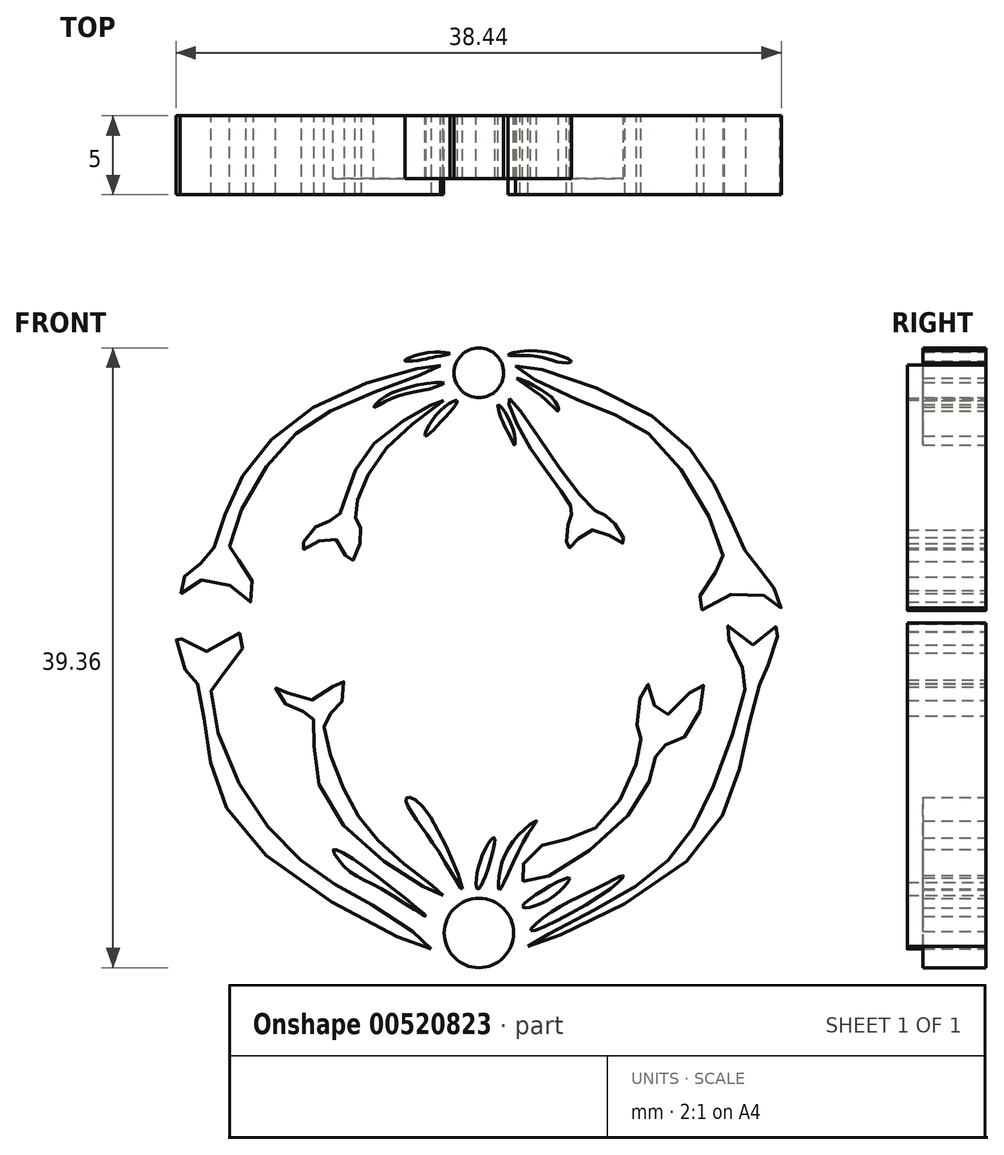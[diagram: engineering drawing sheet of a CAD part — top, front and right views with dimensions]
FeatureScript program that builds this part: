
annotation { "Feature Type Name" : "Feature", "Feature Type Description" : "" }
export const myFeature = defineFeature(function(context is Context, id is Id, definition is map)
    precondition{}
    {
        {
            var Q0;
            Q0=qCreatedBy(makeId("Front.planeOp"),FACE);
            var sketch = newSketch(context, id + "F0", { "sketchPlane" : qUnion([Q0])});
            skLineSegment(sketch, "E0", {"start": v(0, 0) * mm, "end": v(0, 40) * mm});
            skSolve(sketch);
        }
        {
            var Q0;
            Q0=qCreatedBy(makeId("Front.planeOp"),FACE);
            var sketch = newSketch(context, id + "F1", { "sketchPlane" : qUnion([Q0])});
            skArc(sketch, "E1", {"start": v(0, 0) * mm, "mid": v(19.9, 19.93) * mm, "end": v(0, 39.86) * mm});
            skSolve(sketch);
        }
        {
            var Q0;
            Q0=sQuery(id+"F1.wireOp",EDGE,"E1");
            var Q1;
            Q1=sQuery(id+"F0.wireOp",EDGE,"E0");
            revolve(context, id + "F2", {"bodyType" : ToolBodyType.SURFACE, "surfaceEntities" : qUnion([Q0]), "axis" : qUnion([Q1]), "revolveType" : RevolveType.TWO_DIRECTIONS, "angle" : 179.35 * degree, "angleBack" : 1.4 * degree});
        }
        {
            var Q0;
            Q0=qCreatedBy(makeId("Front.planeOp"),FACE);
            var sketch = newSketch(context, id + "F3", { "sketchPlane" : qUnion([Q0])});
            skCircle(sketch, "E2", {"center": v(0, 2.34) * mm, "radius": 2.2 * mm});
            skSolve(sketch);
        }
        {
            var Q0;
            Q0=makeQuery(id+"F3.imprint","IMPRINT",FACE,{"disambiguationData":[TD([[makeQuery(id+"F3.imprint","IMPRINT",EDGE,{"derivedFrom":sQuery(id+"F3.wireOp",EDGE,"E2")}),1.0]])]});
            extrude(context, id + "F4", {"entities" : qUnion([Q0]), "depth" : 4 * mm, "offsetDistance" : 25 * mm});
        }
        {
            var Q0;
            Q0=qCreatedBy(makeId("Front.planeOp"),FACE);
            var sketch = newSketch(context, id + "F5", { "sketchPlane" : qUnion([Q0])});
            skCircle(sketch, "E3", {"center": v(0, 37.92) * mm, "radius": 1.58 * mm});
            skSolve(sketch);
        }
        {
            var Q0;
            Q0=makeQuery(id+"F5.imprint","IMPRINT",FACE,{"disambiguationData":[TD([[makeQuery(id+"F5.imprint","IMPRINT",EDGE,{"derivedFrom":sQuery(id+"F5.wireOp",EDGE,"E3")}),1.0]])]});
            extrude(context, id + "F6", {"entities" : qUnion([Q0]), "depth" : 4 * mm, "offsetDistance" : 25 * mm});
        }
        {
            var Q0;
            Q0=qCreatedBy(makeId("Front.planeOp"),FACE);
            var sketch = newSketch(context, id + "F7", { "sketchPlane" : qUnion([Q0])});
            skFitSpline(sketch, "E4", {"points": [v(2.8, 5.61) * mm, v(10.25, 10.8) * mm, v(11.49, 14.06) * mm, v(13.34, 15.07) * mm, v(14.11, 18.2) * mm, v(11.61, 16.13) * mm, v(10.72, 18.16) * mm, v(10.01, 15.74) * mm, v(10.3, 14.49) * mm, v(7.37, 8.98) * mm, v(3.55, 7.63) * mm, v(2.8, 5.61) * mm]});
            skSolve(sketch);
        }
        {
            var Q0;
            Q0=makeQuery(id+"F7.imprint","IMPRINT",FACE,{"disambiguationData":[TD([[makeQuery(id+"F7.imprint","IMPRINT",EDGE,{"derivedFrom":sQuery(id+"F7.wireOp",EDGE,"E4")}),1.0]])]});
            extrude(context, id + "F8", {"entities" : qUnion([Q0]), "depth" : 5 * mm, "offsetDistance" : 25 * mm});
        }
        {
            var Q0;
            Q0=qCreatedBy(makeId("Front.planeOp"),FACE);
            var sketch = newSketch(context, id + "F9", { "sketchPlane" : qUnion([Q0])});
            skFitSpline(sketch, "E5", {"points": [v(-2.25, 36.18) * mm, v(-7.2, 32.8) * mm, v(-8.95, 28.8) * mm, v(-10.37, 28.13) * mm, v(-11.23, 26.7) * mm, v(-9.3, 27.44) * mm, v(-8.17, 25.93) * mm, v(-7.46, 27.8) * mm, v(-7.83, 28.66) * mm, v(-5.82, 33.2) * mm, v(-2.25, 36.18) * mm]});
            skSolve(sketch);
        }
        {
            var Q0;
            Q0=qCreatedBy(makeId("Front.planeOp"),FACE);
            var sketch = newSketch(context, id + "F10", { "sketchPlane" : qUnion([Q0])});
            skFitSpline(sketch, "E6", {"points": [v(-3.05, 1.35) * mm, v(-13.8, 7.53) * mm, v(-17.31, 14.74) * mm, v(-18.05, 18.51) * mm, v(-18.8, 19.3) * mm, v(-19.2, 21.5) * mm, v(-17.99, 20.17) * mm, v(-14.91, 21.45) * mm, v(-15.64, 19.34) * mm, v(-16.89, 18.24) * mm, v(-15.48, 12.3) * mm, v(-10.79, 6.54) * mm, v(-6.03, 3.66) * mm, v(-3.05, 1.35) * mm]});
            skSolve(sketch);
        }
        {
            var Q0;
            Q0=qCreatedBy(makeId("Front.planeOp"),FACE);
            var sketch = newSketch(context, id + "F11", { "sketchPlane" : qUnion([Q0])});
            skFitSpline(sketch, "E7", {"points": [v(-2.29, 4.72) * mm, v(-9.68, 10.66) * mm, v(-10.63, 16.2) * mm, v(-11.97, 16.64) * mm, v(-12.88, 17.97) * mm, v(-10.66, 17.13) * mm, v(-8.69, 18.42) * mm, v(-8.84, 16.76) * mm, v(-9.74, 16) * mm, v(-8.6, 11.55) * mm, v(-5.28, 7.16) * mm, v(-2.29, 4.72) * mm]});
            skSolve(sketch);
        }
        {
            var Q0;
            Q0=qCreatedBy(makeId("Front.planeOp"),FACE);
            var sketch = newSketch(context, id + "F12", { "sketchPlane" : qUnion([Q0])});
            skFitSpline(sketch, "E8", {"points": [v(3.12, 1.48) * mm, v(12.95, 6.68) * mm, v(16.85, 14.18) * mm, v(18.02, 18.66) * mm, v(18.55, 19.78) * mm, v(19.07, 22.03) * mm, v(17.52, 20.65) * mm, v(15.64, 21.98) * mm, v(16.5, 19.58) * mm, v(16.96, 18.56) * mm, v(15.06, 12.06) * mm, v(11.96, 6.9) * mm, v(6.67, 3.46) * mm, v(3.12, 1.48) * mm]});
            skSolve(sketch);
        }
        {
            var Q0;
            Q0=makeQuery(id+"F10.imprint","IMPRINT",FACE,{"disambiguationData":[TD([[makeQuery(id+"F10.imprint","IMPRINT",EDGE,{"derivedFrom":sQuery(id+"F10.wireOp",EDGE,"E6")}),-1.0]])]});
            extrude(context, id + "F13", {"entities" : qUnion([Q0]), "depth" : 5 * mm, "offsetDistance" : 25 * mm});
        }
        {
            var Q0;
            Q0=makeQuery(id+"F11.imprint","IMPRINT",FACE,{"disambiguationData":[TD([[makeQuery(id+"F11.imprint","IMPRINT",EDGE,{"derivedFrom":sQuery(id+"F11.wireOp",EDGE,"E7")}),-1.0]])]});
            extrude(context, id + "F14", {"entities" : qUnion([Q0]), "depth" : 5 * mm, "offsetDistance" : 25 * mm});
        }
        {
            var Q0;
            Q0=makeQuery(id+"F12.imprint","IMPRINT",FACE,{"disambiguationData":[TD([[makeQuery(id+"F12.imprint","IMPRINT",EDGE,{"derivedFrom":sQuery(id+"F12.wireOp",EDGE,"E8")}),1.0]])]});
            extrude(context, id + "F15", {"entities" : qUnion([Q0]), "depth" : 5 * mm, "offsetDistance" : 25 * mm});
        }
        {
            var Q0;
            Q0=qCreatedBy(makeId("Front.planeOp"),FACE);
            var sketch = newSketch(context, id + "F16", { "sketchPlane" : qUnion([Q0])});
            skFitSpline(sketch, "E9", {"points": [v(-2.43, 38.38) * mm, v(-9.35, 36.35) * mm, v(-15.72, 29.99) * mm, v(-17.26, 26.1) * mm, v(-18.44, 25.37) * mm, v(-18.94, 23.93) * mm, v(-16.87, 24.94) * mm, v(-14.47, 23.38) * mm, v(-14.8, 25.68) * mm, v(-15.78, 26.43) * mm, v(-13.3, 32.25) * mm, v(-7.5, 36.36) * mm, v(-2.43, 38.38) * mm]});
            skSolve(sketch);
        }
        {
            var Q0;
            Q0=qCreatedBy(makeId("Front.planeOp"),FACE);
            var sketch = newSketch(context, id + "F17", { "sketchPlane" : qUnion([Q0])});
            skFitSpline(sketch, "E10", {"points": [v(1.95, 36.3) * mm, v(7.08, 29.43) * mm, v(8.37, 28.63) * mm, v(9.24, 27.1) * mm, v(7.16, 27.94) * mm, v(5.7, 26.8) * mm, v(5.7, 28.47) * mm, v(5.88, 29.31) * mm, v(2.98, 33.63) * mm, v(1.95, 36.3) * mm]});
            skSolve(sketch);
        }
        {
            var Q0;
            Q0=qCreatedBy(makeId("Front.planeOp"),FACE);
            var sketch = newSketch(context, id + "F18", { "sketchPlane" : qUnion([Q0])});
            skFitSpline(sketch, "E11", {"points": [v(2.32, 38.37) * mm, v(10.39, 35.55) * mm, v(15.47, 29.79) * mm, v(17.3, 26.03) * mm, v(18.48, 24.67) * mm, v(19.19, 23) * mm, v(17.16, 24.1) * mm, v(13.93, 22.85) * mm, v(14.7, 24.9) * mm, v(15.52, 26.04) * mm, v(11.61, 33.29) * mm, v(6.44, 36.13) * mm, v(2.32, 38.37) * mm]});
            skSolve(sketch);
        }
        {
            var Q0;
            Q0=makeQuery(id+"F18.imprint","IMPRINT",FACE,{"disambiguationData":[TD([[makeQuery(id+"F18.imprint","IMPRINT",EDGE,{"derivedFrom":sQuery(id+"F18.wireOp",EDGE,"E11")}),-1.0]])]});
            extrude(context, id + "F19", {"entities" : qUnion([Q0]), "depth" : 5 * mm, "offsetDistance" : 25 * mm});
        }
        {
            var Q0;
            Q0=makeQuery(id+"F17.imprint","IMPRINT",FACE,{"disambiguationData":[TD([[makeQuery(id+"F17.imprint","IMPRINT",EDGE,{"derivedFrom":sQuery(id+"F17.wireOp",EDGE,"E10")}),-1.0]])]});
            extrude(context, id + "F20", {"entities" : qUnion([Q0]), "depth" : 5 * mm, "offsetDistance" : 25 * mm});
        }
        {
            var Q0;
            Q0=makeQuery(id+"F16.imprint","IMPRINT",FACE,{"disambiguationData":[TD([[makeQuery(id+"F16.imprint","IMPRINT",EDGE,{"derivedFrom":sQuery(id+"F16.wireOp",EDGE,"E9")}),1.0]])]});
            extrude(context, id + "F21", {"entities" : qUnion([Q0]), "depth" : 5 * mm, "offsetDistance" : 25 * mm});
        }
        {
            var Q0;
            Q0=makeQuery(id+"F9.imprint","IMPRINT",FACE,{"disambiguationData":[TD([[makeQuery(id+"F9.imprint","IMPRINT",EDGE,{"derivedFrom":sQuery(id+"F9.wireOp",EDGE,"E5")}),1.0]])]});
            extrude(context, id + "F22", {"entities" : qUnion([Q0]), "depth" : 5 * mm, "offsetDistance" : 25 * mm});
        }
        {
            var Q0;
            Q0=qCreatedBy(makeId("Front.planeOp"),FACE);
            var sketch = newSketch(context, id + "F23", { "sketchPlane" : qUnion([Q0])});
            skFitSpline(sketch, "E12", {"points": [v(2.4, 37.58) * mm, v(4.66, 36.3) * mm, v(5.02, 35.51) * mm, v(4.12, 36.32) * mm, v(2.4, 37.58) * mm]});
            skSolve(sketch);
        }
        {
            var Q0;
            Q0=qCreatedBy(makeId("Front.planeOp"),FACE);
            var sketch = newSketch(context, id + "F24", { "sketchPlane" : qUnion([Q0])});
            skFitSpline(sketch, "E13", {"points": [v(1.23, 35.9) * mm, v(2.12, 34.46) * mm, v(2.26, 33.34) * mm, v(1.99, 33.86) * mm, v(1.43, 34.99) * mm, v(1.23, 35.9) * mm]});
            skSolve(sketch);
        }
        {
            var Q0;
            Q0=qCreatedBy(makeId("Front.planeOp"),FACE);
            var sketch = newSketch(context, id + "F25", { "sketchPlane" : qUnion([Q0])});
            skFitSpline(sketch, "E14", {"points": [v(-1.85, 39.14) * mm, v(-3.37, 39.19) * mm, v(-4.7, 38.7) * mm, v(-3.66, 38.75) * mm, v(-2.75, 38.95) * mm, v(-1.85, 39.14) * mm]});
            skSolve(sketch);
        }
        {
            var Q0;
            Q0=qCreatedBy(makeId("Front.planeOp"),FACE);
            var sketch = newSketch(context, id + "F26", { "sketchPlane" : qUnion([Q0])});
            skFitSpline(sketch, "E15", {"points": [v(-2.22, 37.28) * mm, v(-4.02, 37.12) * mm, v(-6.27, 36.2) * mm, v(-6.68, 35.74) * mm, v(-5.52, 36.3) * mm, v(-3.34, 36.86) * mm, v(-2.22, 37.28) * mm]});
            skSolve(sketch);
        }
        {
            var Q0;
            Q0=qCreatedBy(makeId("Front.planeOp"),FACE);
            var sketch = newSketch(context, id + "F27", { "sketchPlane" : qUnion([Q0])});
            skFitSpline(sketch, "E16", {"points": [v(-1.38, 36.16) * mm, v(-2.64, 35.33) * mm, v(-3.4, 33.92) * mm, v(-2.4, 34.83) * mm, v(-1.38, 36.16) * mm]});
            skSolve(sketch);
        }
        {
            var Q0;
            Q0=qCreatedBy(makeId("Front.planeOp"),FACE);
            var sketch = newSketch(context, id + "F28", { "sketchPlane" : qUnion([Q0])});
            skFitSpline(sketch, "E17", {"points": [v(1.85, 39.07) * mm, v(3.7, 39.32) * mm, v(5.86, 38.64) * mm, v(5.08, 38.6) * mm, v(3.68, 38.97) * mm, v(1.85, 39.07) * mm]});
            skSolve(sketch);
        }
        {
            var Q0;
            Q0=makeQuery(id+"F25.imprint","IMPRINT",FACE,{"disambiguationData":[TD([[makeQuery(id+"F25.imprint","IMPRINT",EDGE,{"derivedFrom":sQuery(id+"F25.wireOp",EDGE,"E14")}),1.0]])]});
            extrude(context, id + "F29", {"entities" : qUnion([Q0]), "depth" : 4 * mm, "offsetDistance" : 25 * mm});
        }
        {
            var Q0;
            Q0=makeQuery(id+"F26.imprint","IMPRINT",FACE,{"disambiguationData":[TD([[makeQuery(id+"F26.imprint","IMPRINT",EDGE,{"derivedFrom":sQuery(id+"F26.wireOp",EDGE,"E15")}),1.0]])]});
            extrude(context, id + "F30", {"entities" : qUnion([Q0]), "depth" : 4 * mm, "offsetDistance" : 25 * mm});
        }
        {
            var Q0;
            Q0=makeQuery(id+"F27.imprint","IMPRINT",FACE,{"disambiguationData":[TD([[makeQuery(id+"F27.imprint","IMPRINT",EDGE,{"derivedFrom":sQuery(id+"F27.wireOp",EDGE,"E16")}),1.0]])]});
            extrude(context, id + "F31", {"entities" : qUnion([Q0]), "depth" : 4 * mm, "offsetDistance" : 25 * mm});
        }
        {
            var Q0;
            Q0=makeQuery(id+"F24.imprint","IMPRINT",FACE,{"disambiguationData":[TD([[makeQuery(id+"F24.imprint","IMPRINT",EDGE,{"derivedFrom":sQuery(id+"F24.wireOp",EDGE,"E13")}),-1.0]])]});
            extrude(context, id + "F32", {"entities" : qUnion([Q0]), "depth" : 4 * mm, "offsetDistance" : 25 * mm});
        }
        {
            var Q0;
            Q0=makeQuery(id+"F28.imprint","IMPRINT",FACE,{"disambiguationData":[TD([[makeQuery(id+"F28.imprint","IMPRINT",EDGE,{"derivedFrom":sQuery(id+"F28.wireOp",EDGE,"E17")}),-1.0]])]});
            extrude(context, id + "F33", {"entities" : qUnion([Q0]), "depth" : 4 * mm, "offsetDistance" : 25 * mm});
        }
        {
            var Q0;
            Q0=makeQuery(id+"F23.imprint","IMPRINT",FACE,{"disambiguationData":[TD([[makeQuery(id+"F23.imprint","IMPRINT",EDGE,{"derivedFrom":sQuery(id+"F23.wireOp",EDGE,"E12")}),-1.0]])]});
            extrude(context, id + "F34", {"entities" : qUnion([Q0]), "depth" : 4 * mm, "offsetDistance" : 25 * mm});
        }
        {
            var Q0;
            Q0=qCreatedBy(makeId("Front.planeOp"),FACE);
            var sketch = newSketch(context, id + "F35", { "sketchPlane" : qUnion([Q0])});
            skFitSpline(sketch, "E18", {"points": [v(3.3, 2.47) * mm, v(8.25, 5.09) * mm, v(9.15, 5.99) * mm, v(7.53, 5.2) * mm, v(4.38, 3.53) * mm, v(3.3, 2.47) * mm]});
            skSolve(sketch);
        }
        {
            var Q0;
            Q0=qCreatedBy(makeId("Front.planeOp"),FACE);
            var sketch = newSketch(context, id + "F36", { "sketchPlane" : qUnion([Q0])});
            skFitSpline(sketch, "E19", {"points": [v(-3.37, 3.4) * mm, v(-7.54, 6.72) * mm, v(-9.26, 7.6) * mm, v(-8.32, 6.35) * mm, v(-6.23, 5.17) * mm, v(-3.37, 3.4) * mm]});
            skSolve(sketch);
        }
        {
            var Q0;
            Q0=qCreatedBy(makeId("Front.planeOp"),FACE);
            var sketch = newSketch(context, id + "F37", { "sketchPlane" : qUnion([Q0])});
            skFitSpline(sketch, "E20", {"points": [v(1.3, 5.09) * mm, v(2.83, 8.15) * mm, v(3.65, 9.46) * mm, v(2.3, 8.34) * mm, v(1.3, 6.07) * mm, v(1.3, 5.09) * mm]});
            skSolve(sketch);
        }
        {
            var Q0;
            Q0=qCreatedBy(makeId("Front.planeOp"),FACE);
            var sketch = newSketch(context, id + "F38", { "sketchPlane" : qUnion([Q0])});
            skFitSpline(sketch, "E21", {"points": [v(-1.06, 5.15) * mm, v(-3.61, 10.42) * mm, v(-4.62, 10.9) * mm, v(-4.2, 9.9) * mm, v(-2.37, 7.2) * mm, v(-1.06, 5.15) * mm]});
            skSolve(sketch);
        }
        {
            var Q0;
            Q0=makeQuery(id+"F38.imprint","IMPRINT",FACE,{"disambiguationData":[TD([[makeQuery(id+"F38.imprint","IMPRINT",EDGE,{"derivedFrom":sQuery(id+"F38.wireOp",EDGE,"E21")}),1.0]])]});
            extrude(context, id + "F39", {"entities" : qUnion([Q0]), "depth" : 4 * mm, "offsetDistance" : 25 * mm});
        }
        {
            var Q0;
            Q0=makeQuery(id+"F37.imprint","IMPRINT",FACE,{"disambiguationData":[TD([[makeQuery(id+"F37.imprint","IMPRINT",EDGE,{"derivedFrom":sQuery(id+"F37.wireOp",EDGE,"E20")}),1.0]])]});
            extrude(context, id + "F40", {"entities" : qUnion([Q0]), "depth" : 4 * mm, "offsetDistance" : 25 * mm});
        }
        {
            var Q0;
            Q0=makeQuery(id+"F35.imprint","IMPRINT",FACE,{"disambiguationData":[TD([[makeQuery(id+"F35.imprint","IMPRINT",EDGE,{"derivedFrom":sQuery(id+"F35.wireOp",EDGE,"E18")}),1.0]])]});
            extrude(context, id + "F41", {"entities" : qUnion([Q0]), "depth" : 4 * mm, "offsetDistance" : 25 * mm});
        }
        {
            var Q0;
            Q0=makeQuery(id+"F36.imprint","IMPRINT",FACE,{"disambiguationData":[TD([[makeQuery(id+"F36.imprint","IMPRINT",EDGE,{"derivedFrom":sQuery(id+"F36.wireOp",EDGE,"E19")}),1.0]])]});
            extrude(context, id + "F42", {"entities" : qUnion([Q0]), "depth" : 4 * mm, "offsetDistance" : 25 * mm});
        }
        {
            var Q0;
            Q0=qCreatedBy(makeId("Front.planeOp"),FACE);
            var sketch = newSketch(context, id + "F43", { "sketchPlane" : qUnion([Q0])});
            skFitSpline(sketch, "E22", {"points": [v(0, 5.18) * mm, v(1, 8.34) * mm, v(0, 6.67) * mm, v(0, 5.18) * mm]});
            skSolve(sketch);
        }
        {
            var Q0;
            Q0=qCreatedBy(makeId("Front.planeOp"),FACE);
            var sketch = newSketch(context, id + "F44", { "sketchPlane" : qUnion([Q0])});
            skFitSpline(sketch, "E23", {"points": [v(2.78, 4.07) * mm, v(5.7, 5.85) * mm, v(5.2, 5.08) * mm, v(3.45, 4.03) * mm, v(2.78, 4.07) * mm]});
            skSolve(sketch);
        }
        {
            var Q0;
            Q0=makeQuery(id+"F44.imprint","IMPRINT",FACE,{"disambiguationData":[TD([[makeQuery(id+"F44.imprint","IMPRINT",EDGE,{"derivedFrom":sQuery(id+"F44.wireOp",EDGE,"E23")}),-1.0]])]});
            extrude(context, id + "F45", {"entities" : qUnion([Q0]), "depth" : 4 * mm, "offsetDistance" : 25 * mm});
        }
        {
            var Q0;
            Q0=makeQuery(id+"F43.imprint","IMPRINT",FACE,{"disambiguationData":[TD([[makeQuery(id+"F43.imprint","IMPRINT",EDGE,{"derivedFrom":sQuery(id+"F43.wireOp",EDGE,"E22")}),1.0]])]});
            extrude(context, id + "F46", {"entities" : qUnion([Q0]), "depth" : 4 * mm, "offsetDistance" : 25 * mm});
        }
        {
            var Q0;
            Q0=qCreatedBy(makeId("Front.planeOp"),FACE);
            var sketch = newSketch(context, id + "F47", { "sketchPlane" : qUnion([Q0])});
            skCircle(sketch, "E24", {"center": v(0, 37.76) * mm, "radius": 0.4 * mm});
            skSolve(sketch);
        }
        {
            var Q0;
            Q0=sQuery(id+"F47.wireOp",EDGE,"E24");
            extrude(context, id + "F48", {"bodyType" : ToolBodyType.SURFACE, "surfaceEntities" : qUnion([Q0]), "depth" : 5 * mm, "offsetDistance" : 25 * mm});
        }
        {
            var Q0;
            Q0=qCreatedBy(makeId("Front.planeOp"),FACE);
            var sketch = newSketch(context, id + "F49", { "sketchPlane" : qUnion([Q0])});
            skCircle(sketch, "E25", {"center": v(0.52, 38.47) * mm, "radius": 0.3 * mm});
            skSolve(sketch);
        }
        {
            var Q0;
            Q0=sQuery(id+"F49.wireOp",EDGE,"E25");
            extrude(context, id + "F50", {"bodyType" : ToolBodyType.SURFACE, "surfaceEntities" : qUnion([Q0]), "depth" : 5 * mm, "offsetDistance" : 25 * mm});
        }
        {
            var Q0;
            Q0=qCreatedBy(makeId("Front.planeOp"),FACE);
            var sketch = newSketch(context, id + "F51", { "sketchPlane" : qUnion([Q0])});
            skCircle(sketch, "E26", {"center": v(-0.28, 3.47) * mm, "radius": 0.89 * mm});
            skSolve(sketch);
        }
        {
            var Q0;
            Q0=qCreatedBy(makeId("Front.planeOp"),FACE);
            var sketch = newSketch(context, id + "F52", { "sketchPlane" : qUnion([Q0])});
            skCircle(sketch, "E27", {"center": v(0.81, 1.96) * mm, "radius": 0.5 * mm});
            skSolve(sketch);
        }
        {
            var Q0;
            Q0=sQuery(id+"F51.wireOp",EDGE,"E26");
            extrude(context, id + "F53", {"bodyType" : ToolBodyType.SURFACE, "surfaceEntities" : qUnion([Q0]), "depth" : 5 * mm, "offsetDistance" : 25 * mm});
        }
        {
            var Q0;
            Q0=sQuery(id+"F52.wireOp",EDGE,"E27");
            extrude(context, id + "F54", {"bodyType" : ToolBodyType.SURFACE, "surfaceEntities" : qUnion([Q0]), "depth" : 5 * mm, "offsetDistance" : 25 * mm});
        }
        {
            var Q0;
            Q0=qCreatedBy(makeId("Front.planeOp"),FACE);
            var sketch = newSketch(context, id + "F55", { "sketchPlane" : qUnion([Q0])});
            skCircle(sketch, "E28", {"center": v(-16.18, 26.96) * mm, "radius": 0.54 * mm});
            skSolve(sketch);
        }
        {
            var Q0;
            Q0=qCreatedBy(makeId("Front.planeOp"),FACE);
            var sketch = newSketch(context, id + "F56", { "sketchPlane" : qUnion([Q0])});
            skCircle(sketch, "E29", {"center": v(-8.3, 29.19) * mm, "radius": 0.58 * mm});
            skSolve(sketch);
        }
        {
            var Q0;
            Q0=sQuery(id+"F56.wireOp",EDGE,"E29");
            extrude(context, id + "F57", {"bodyType" : ToolBodyType.SURFACE, "surfaceEntities" : qUnion([Q0]), "depth" : 6 * mm, "offsetDistance" : 25 * mm});
        }
        {
            var Q0;
            Q0=sQuery(id+"F55.wireOp",EDGE,"E28");
            extrude(context, id + "F58", {"bodyType" : ToolBodyType.SURFACE, "surfaceEntities" : qUnion([Q0]), "depth" : 6 * mm, "offsetDistance" : 25 * mm});
        }
        {
            var Q0;
            Q0=qCreatedBy(makeId("Front.planeOp"),FACE);
            var sketch = newSketch(context, id + "F59", { "sketchPlane" : qUnion([Q0])});
            skCircle(sketch, "E30", {"center": v(6.33, 29.3) * mm, "radius": 0.73 * mm});
            skSolve(sketch);
        }
        {
            var Q0;
            Q0=qCreatedBy(makeId("Front.planeOp"),FACE);
            var sketch = newSketch(context, id + "F60", { "sketchPlane" : qUnion([Q0])});
            skCircle(sketch, "E31", {"center": v(16.17, 26.01) * mm, "radius": 0.97 * mm});
            skSolve(sketch);
        }
        {
            var Q0;
            Q0=sQuery(id+"F59.wireOp",EDGE,"E30");
            extrude(context, id + "F61", {"bodyType" : ToolBodyType.SURFACE, "surfaceEntities" : qUnion([Q0]), "depth" : 6 * mm, "offsetDistance" : 25 * mm});
        }
        {
            var Q0;
            Q0=sQuery(id+"F60.wireOp",EDGE,"E31");
            extrude(context, id + "F62", {"bodyType" : ToolBodyType.SURFACE, "surfaceEntities" : qUnion([Q0]), "depth" : 6 * mm, "offsetDistance" : 25 * mm});
        }
        {
            var Q0;
            Q0=qCreatedBy(makeId("Front.planeOp"),FACE);
            var sketch = newSketch(context, id + "F63", { "sketchPlane" : qUnion([Q0])});
            skCircle(sketch, "E32", {"center": v(-10.1, 15.44) * mm, "radius": 0.94 * mm});
            skSolve(sketch);
        }
        {
            var Q0;
            Q0=qCreatedBy(makeId("Front.planeOp"),FACE);
            var sketch = newSketch(context, id + "F64", { "sketchPlane" : qUnion([Q0])});
            skCircle(sketch, "E33", {"center": v(-17.08, 17.65) * mm, "radius": 1.16 * mm});
            skSolve(sketch);
        }
        {
            var Q0;
            Q0=sQuery(id+"F63.wireOp",EDGE,"E32");
            extrude(context, id + "F65", {"bodyType" : ToolBodyType.SURFACE, "surfaceEntities" : qUnion([Q0]), "depth" : 6 * mm, "offsetDistance" : 25 * mm});
        }
        {
            var Q0;
            Q0=sQuery(id+"F64.wireOp",EDGE,"E33");
            extrude(context, id + "F66", {"bodyType" : ToolBodyType.SURFACE, "surfaceEntities" : qUnion([Q0]), "depth" : 6 * mm, "offsetDistance" : 25 * mm});
        }
        {
            var Q0;
            Q0=qCreatedBy(makeId("Front.planeOp"),FACE);
            var sketch = newSketch(context, id + "F67", { "sketchPlane" : qUnion([Q0])});
            skCircle(sketch, "E34", {"center": v(10.94, 14) * mm, "radius": 1.05 * mm});
            skSolve(sketch);
        }
        {
            var Q0;
            Q0=qCreatedBy(makeId("Front.planeOp"),FACE);
            var sketch = newSketch(context, id + "F68", { "sketchPlane" : qUnion([Q0])});
            skCircle(sketch, "E35", {"center": v(17.24, 18.67) * mm, "radius": 1.1 * mm});
            skSolve(sketch);
        }
        {
            var Q0;
            Q0=sQuery(id+"F68.wireOp",EDGE,"E35");
            extrude(context, id + "F69", {"bodyType" : ToolBodyType.SURFACE, "surfaceEntities" : qUnion([Q0]), "depth" : 6 * mm, "offsetDistance" : 25 * mm});
        }
        {
            var Q0;
            Q0=sQuery(id+"F67.wireOp",EDGE,"E34");
            extrude(context, id + "F70", {"bodyType" : ToolBodyType.SURFACE, "surfaceEntities" : qUnion([Q0]), "depth" : 6 * mm, "offsetDistance" : 25 * mm});
        }
    });
